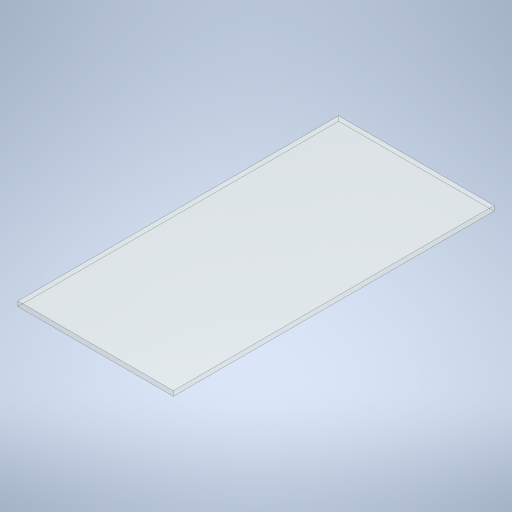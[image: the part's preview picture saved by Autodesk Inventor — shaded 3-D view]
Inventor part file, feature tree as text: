
AUTODESK INVENTOR PART (.ipt)
format: ipt  version: 2023 (Build 270158000, 158)  size: 222,720 bytes
history: native  units: in
note: dims shown in document units (in); Inventor stores cm internally (conversion verified against a paired STEP export)
features: extrude x1, sketch x1
ambient origin geometry x8: Origin, YZ Plane, XZ Plane, XY Plane, X Axis, Y Axis, Z Axis, Center Point
bodies: Solid1 (feature_tree)
feature tree (2):
  extrude  "Extrusion1"  Depth=16.5in
  sketch  "Sketch1"  dims[d0=8.0in d1=16.5in d2=0.25in d3=0.0in]
